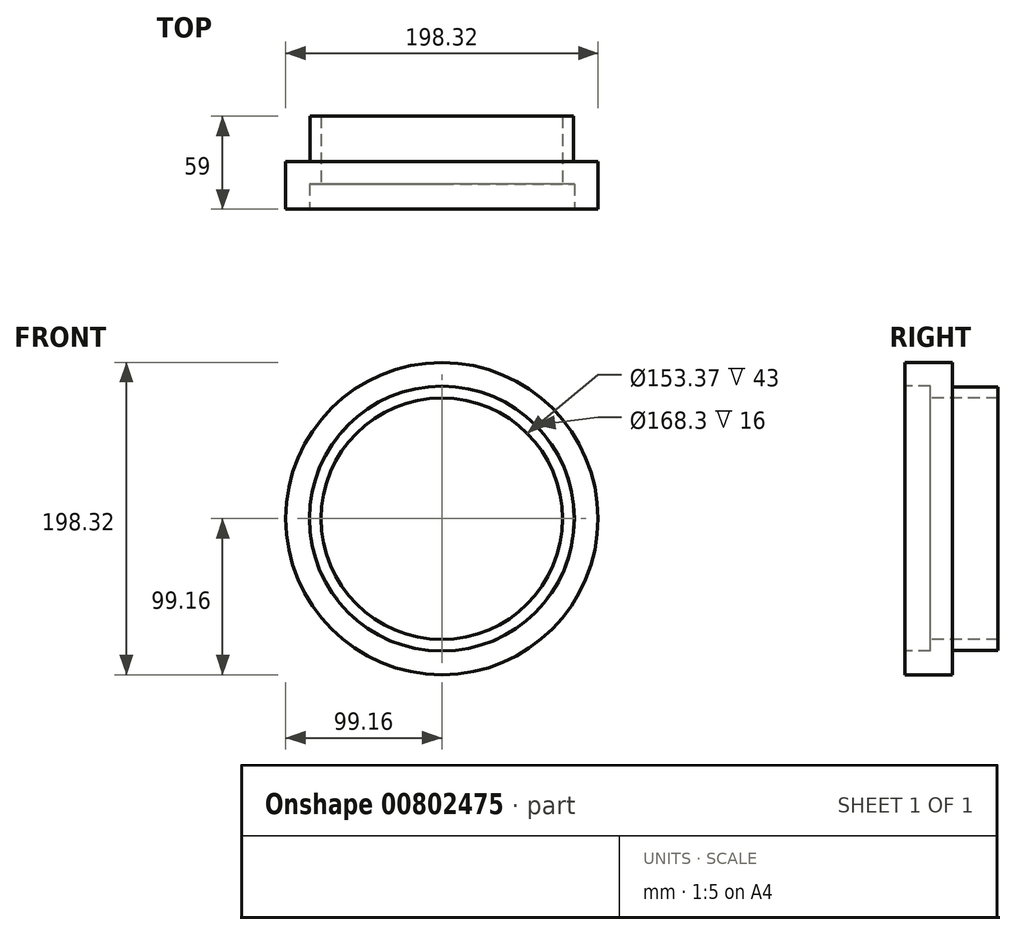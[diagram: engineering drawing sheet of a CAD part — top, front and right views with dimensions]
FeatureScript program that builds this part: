
annotation { "Feature Type Name" : "Feature", "Feature Type Description" : "" }
export const myFeature = defineFeature(function(context is Context, id is Id, definition is map)
    precondition{}
    {
        {
            var Q0;
            Q0=qCreatedBy(makeId("Front.planeOp"),FACE);
            var sketch = newSketch(context, id + "F0", { "sketchPlane" : qUnion([Q0])});
            skCircle(sketch, "E0", {"center": v(0, 0) * mm, "radius": 83.69 * mm});
            skCircle(sketch, "E1.0", {"center": v(0, 0) * mm, "radius": 98.69 * mm});
            skCircle(sketch, "E2.0", {"center": v(0, 0) * mm, "radius": 76.69 * mm});
            skSolve(sketch);
        }
        {
            var Q0;
            Q0=makeQuery(id+"F0.imprint","IMPRINT",FACE,{"disambiguationData":[TD([[makeQuery(id+"F0.imprint","IMPRINT",EDGE,{"derivedFrom":sQuery(id+"F0.wireOp",EDGE,"E0")}),-1.0]])]});
            extrude(context, id + "F1", {"entities" : qUnion([Q0]), "depth" : 16 * mm, "offsetDistance" : 25 * mm});
        }
        {
            var Q0;
            Q0=makeQuery(id+"F0.imprint","IMPRINT",FACE,{"disambiguationData":[TD([[makeQuery(id+"F0.imprint","IMPRINT",EDGE,{"derivedFrom":sQuery(id+"F0.wireOp",EDGE,"E0")}),1.0]])]});
            var Q1;
            Q1=makeQuery(id+"F0.imprint","IMPRINT",FACE,{"disambiguationData":[TD([[makeQuery(id+"F0.imprint","IMPRINT",EDGE,{"derivedFrom":sQuery(id+"F0.wireOp",EDGE,"E0")}),-1.0]])]});
            extrude(context, id + "F2", {"entities" : qUnion([Q0, Q1]), "operationType" : NewBodyOperationType.ADD, "oppositeDirection" : true, "depth" : 14 * mm, "offsetDistance" : 25 * mm});
        }
        {
            var Q0;
            Q0=makeQuery(id+"F0.imprint","IMPRINT",FACE,{"disambiguationData":[TD([[makeQuery(id+"F0.imprint","IMPRINT",EDGE,{"derivedFrom":sQuery(id+"F0.wireOp",EDGE,"E0")}),1.0]])]});
            extrude(context, id + "F3", {"entities" : qUnion([Q0]), "operationType" : NewBodyOperationType.ADD, "oppositeDirection" : true, "depth" : 43 * mm, "offsetDistance" : 25 * mm});
        }
        {
            var Q0;
            Q0=makeQuery(id+"F1.opExtrude","CAP_FACE",FACE,{"disambiguationData":[OSD([sQuery(id+"F0.wireOp",EDGE,"E0"),sQuery(id+"F0.wireOp",EDGE,"E1.0")])],"isStart":false});
            var sketch = newSketch(context, id + "F4", { "sketchPlane" : qUnion([Q0])});
            skCircle(sketch, "E3", {"center": v(0, 0) * mm, "radius": 83.65 * mm});
            skCircle(sketch, "E4.0", {"center": v(0, 0) * mm, "radius": 84.15 * mm});
            skSolve(sketch);
        }
        {
            var Q0;
            Q0=makeQuery(id+"F4.imprint","IMPRINT",FACE,{"disambiguationData":[TD([[makeQuery(id+"F4.imprint","IMPRINT",EDGE,{"derivedFrom":sQuery(id+"F4.wireOp",EDGE,"E4.0")}),1.0]])]});
            extrude(context, id + "F5", {"entities" : qUnion([Q0]), "operationType" : NewBodyOperationType.REMOVE, "oppositeDirection" : true, "depth" : 16 * mm, "offsetDistance" : 25 * mm});
        }
        {
            var Q0;
            Q0=makeQuery(id+"F1.opExtrude","CAP_FACE",FACE,{"disambiguationData":[OSD([sQuery(id+"F0.wireOp",EDGE,"E0"),sQuery(id+"F0.wireOp",EDGE,"E1.0")])],"isStart":false});
            var sketch = newSketch(context, id + "F6", { "sketchPlane" : qUnion([Q0])});
            skCircle(sketch, "E5", {"center": v(0, 0) * mm, "radius": 98.66 * mm});
            skCircle(sketch, "E6.0", {"center": v(0, 0) * mm, "radius": 99.16 * mm});
            skSolve(sketch);
        }
        {
            var Q0;
            Q0=makeQuery(id+"F6.imprint","IMPRINT",FACE,{"disambiguationData":[TD([[makeQuery(id+"F6.imprint","IMPRINT",EDGE,{"derivedFrom":sQuery(id+"F6.wireOp",EDGE,"E6.0")}),1.0]])]});
            extrude(context, id + "F7", {"entities" : qUnion([Q0]), "operationType" : NewBodyOperationType.ADD, "oppositeDirection" : true, "depth" : 30 * mm, "offsetDistance" : 25 * mm});
        }
    });
